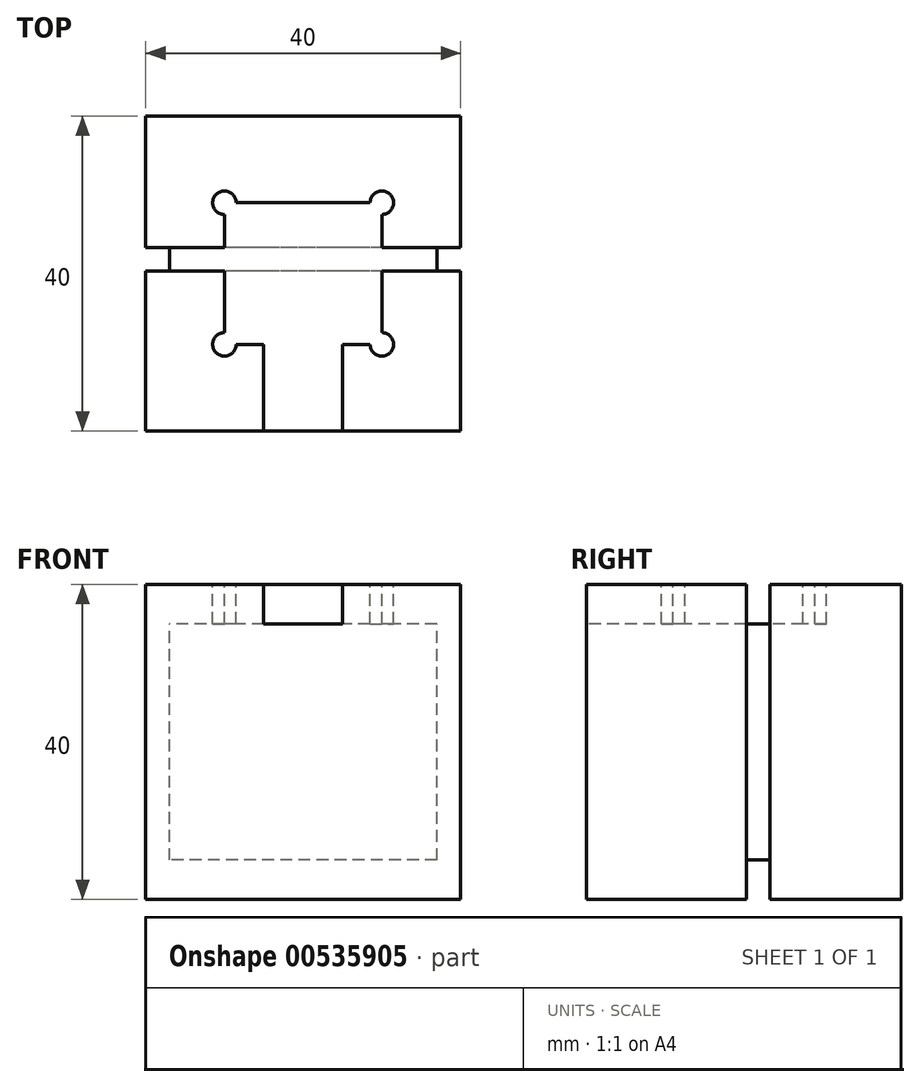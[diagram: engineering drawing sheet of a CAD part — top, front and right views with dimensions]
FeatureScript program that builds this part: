
annotation { "Feature Type Name" : "Feature", "Feature Type Description" : "" }
export const myFeature = defineFeature(function(context is Context, id is Id, definition is map)
    precondition{}
    {
        {
            var Q0;
            Q0=qCreatedBy(makeId("Top.planeOp"),FACE);
            var sketch = newSketch(context, id + "F0", { "sketchPlane" : qUnion([Q0])});
            skLineSegment(sketch, "E0.bottom", {"start": v(20, 20) * mm, "end": v(-20, 20) * mm});
            skLineSegment(sketch, "E0.top", {"start": v(20, -20) * mm, "end": v(-20, -20) * mm});
            skLineSegment(sketch, "E0.left", {"start": v(20, 20) * mm, "end": v(20, -20) * mm});
            skLineSegment(sketch, "E0.right", {"start": v(-20, 20) * mm, "end": v(-20, -20) * mm});
            skPoint(sketch, "E0.middle", {"position": v(0, 0) * mm});
            skSolve(sketch);
        }
        {
            var Q0;
            Q0 = qSketchRegion(id + "F0", true);
            extrude(context, id + "F1", {"entities" : qUnion([Q0]), "depth" : 40 * mm, "offsetDistance" : 25 * mm});
        }
        {
            var Q0;
            Q0=makeQuery(id+"F1.opExtrude","CAP_FACE",FACE,{"disambiguationData":[OSD([sQuery(id+"F0.wireOp",EDGE,"E0.bottom"),sQuery(id+"F0.wireOp",EDGE,"E0.top"),sQuery(id+"F0.wireOp",EDGE,"E0.left"),sQuery(id+"F0.wireOp",EDGE,"E0.right")])],"isStart":false});
            var sketch = newSketch(context, id + "F2", { "sketchPlane" : qUnion([Q0])});
            skLineSegment(sketch, "E1.bottom", {"start": v(10, 9) * mm, "end": v(-10, 9) * mm});
            skLineSegment(sketch, "E1.top", {"start": v(10, -9) * mm, "end": v(-10, -9) * mm});
            skLineSegment(sketch, "E1.left", {"start": v(10, 9) * mm, "end": v(10, -9) * mm});
            skLineSegment(sketch, "E1.right", {"start": v(-10, 9) * mm, "end": v(-10, -9) * mm});
            skPoint(sketch, "E1.middle", {"position": v(0, 0) * mm});
            skCircle(sketch, "E2", {"center": v(-10, 9) * mm, "radius": 1.5 * mm});
            skCircle(sketch, "E3", {"center": v(10, 9) * mm, "radius": 1.5 * mm});
            skCircle(sketch, "E4", {"center": v(10, -9) * mm, "radius": 1.5 * mm});
            skCircle(sketch, "E5", {"center": v(-10, -9) * mm, "radius": 1.5 * mm});
            skLineSegment(sketch, "E6.bottom", {"start": v(-5, -9) * mm, "end": v(5, -9) * mm});
            skLineSegment(sketch, "E6.top", {"start": v(-5, -20) * mm, "end": v(5, -20) * mm});
            skLineSegment(sketch, "E6.left", {"start": v(-5, -9) * mm, "end": v(-5, -20) * mm});
            skLineSegment(sketch, "E6.right", {"start": v(5, -9) * mm, "end": v(5, -20) * mm});
            skLineSegment(sketch, "E7", {"start": v(0, 0) * mm, "end": v(0, -20) * mm, "construction": true});
            skSolve(sketch);
        }
        {
            var Q0;
            Q0 = qSketchRegion(id + "F2", true);
            extrude(context, id + "F3", {"entities" : qUnion([Q0]), "operationType" : NewBodyOperationType.REMOVE, "oppositeDirection" : true, "depth" : 5 * mm, "offsetDistance" : 25 * mm});
        }
        {
            var Q0;
            Q0=makeQuery(id+"F1.opExtrude","CAP_FACE",FACE,{"disambiguationData":[OSD([sQuery(id+"F0.wireOp",EDGE,"E0.bottom"),sQuery(id+"F0.wireOp",EDGE,"E0.top"),sQuery(id+"F0.wireOp",EDGE,"E0.left"),sQuery(id+"F0.wireOp",EDGE,"E0.right")])],"isStart":false});
            var sketch = newSketch(context, id + "F4", { "sketchPlane" : qUnion([Q0])});
            skLineSegment(sketch, "E8.bottom", {"start": v(-20, 3.3) * mm, "end": v(-17, 3.3) * mm});
            skLineSegment(sketch, "E8.top", {"start": v(-20, 0.3) * mm, "end": v(-17, 0.3) * mm});
            skLineSegment(sketch, "E8.left", {"start": v(-20, 3.3) * mm, "end": v(-20, 0.3) * mm});
            skLineSegment(sketch, "E8.right", {"start": v(-17, 3.3) * mm, "end": v(-17, 0.3) * mm});
            skLineSegment(sketch, "E9.bottom", {"start": v(20, 3.3) * mm, "end": v(17, 3.3) * mm});
            skLineSegment(sketch, "E9.top", {"start": v(20, 0.3) * mm, "end": v(17, 0.3) * mm});
            skLineSegment(sketch, "E9.left", {"start": v(20, 3.3) * mm, "end": v(20, 0.3) * mm});
            skLineSegment(sketch, "E9.right", {"start": v(17, 3.3) * mm, "end": v(17, 0.3) * mm});
            skLineSegment(sketch, "E10", {"start": v(-20, 1.8) * mm, "end": v(20, 1.8) * mm, "construction": true});
            skLineSegment(sketch, "E11", {"start": v(0, 17.36) * mm, "end": v(0, -20.04) * mm, "construction": true});
            skSolve(sketch);
        }
        {
            var Q0;
            Q0 = qSketchRegion(id + "F4", true);
            extrude(context, id + "F5", {"entities" : qUnion([Q0]), "operationType" : NewBodyOperationType.REMOVE, "endBound" : BoundingType.THROUGH_ALL, "oppositeDirection" : true, "depth" : 25 * mm, "offsetDistance" : 25 * mm});
        }
        {
            var Q0;
            {var subQ0=sQuery(id+"F0.wireOp",EDGE,"E0.right");var subQ2=sQuery(id+"F0.wireOp",EDGE,"E0.top");Q0=makeQuery(id+"F5.boolean.opBoolean","SPLIT",FACE,{"disambiguationData":[TD([makeQuery(id+"F1.opExtrude","SWEPT_FACE",FACE,{"disambiguationData":[OSD([subQ2])]})])],"derivedFrom":makeQuery(id+"F1.opExtrude","SWEPT_FACE",FACE,{"disambiguationData":[OSD([subQ0])]})});}
            var sketch = newSketch(context, id + "F6", { "sketchPlane" : qUnion([Q0])});
            skLineSegment(sketch, "E12.bottom", {"start": v(-0.3, 40) * mm, "end": v(-3.3, 40) * mm});
            skLineSegment(sketch, "E12.top", {"start": v(-0.3, 35) * mm, "end": v(-3.3, 35) * mm});
            skLineSegment(sketch, "E12.left", {"start": v(-0.3, 40) * mm, "end": v(-0.3, 35) * mm});
            skLineSegment(sketch, "E12.right", {"start": v(-3.3, 40) * mm, "end": v(-3.3, 35) * mm});
            skLineSegment(sketch, "E13.bottom", {"start": v(-0.3, 0) * mm, "end": v(-3.3, 0) * mm});
            skLineSegment(sketch, "E13.top", {"start": v(-0.3, 5) * mm, "end": v(-3.3, 5) * mm});
            skLineSegment(sketch, "E13.left", {"start": v(-0.3, 0) * mm, "end": v(-0.3, 5) * mm});
            skLineSegment(sketch, "E13.right", {"start": v(-3.3, 0) * mm, "end": v(-3.3, 5) * mm});
            skSolve(sketch);
        }
        {
            var Q0;
            Q0 = qSketchRegion(id + "F6", true);
            extrude(context, id + "F7", {"entities" : qUnion([Q0]), "operationType" : NewBodyOperationType.REMOVE, "endBound" : BoundingType.THROUGH_ALL, "oppositeDirection" : true, "depth" : 25 * mm, "offsetDistance" : 25 * mm});
        }
    });
